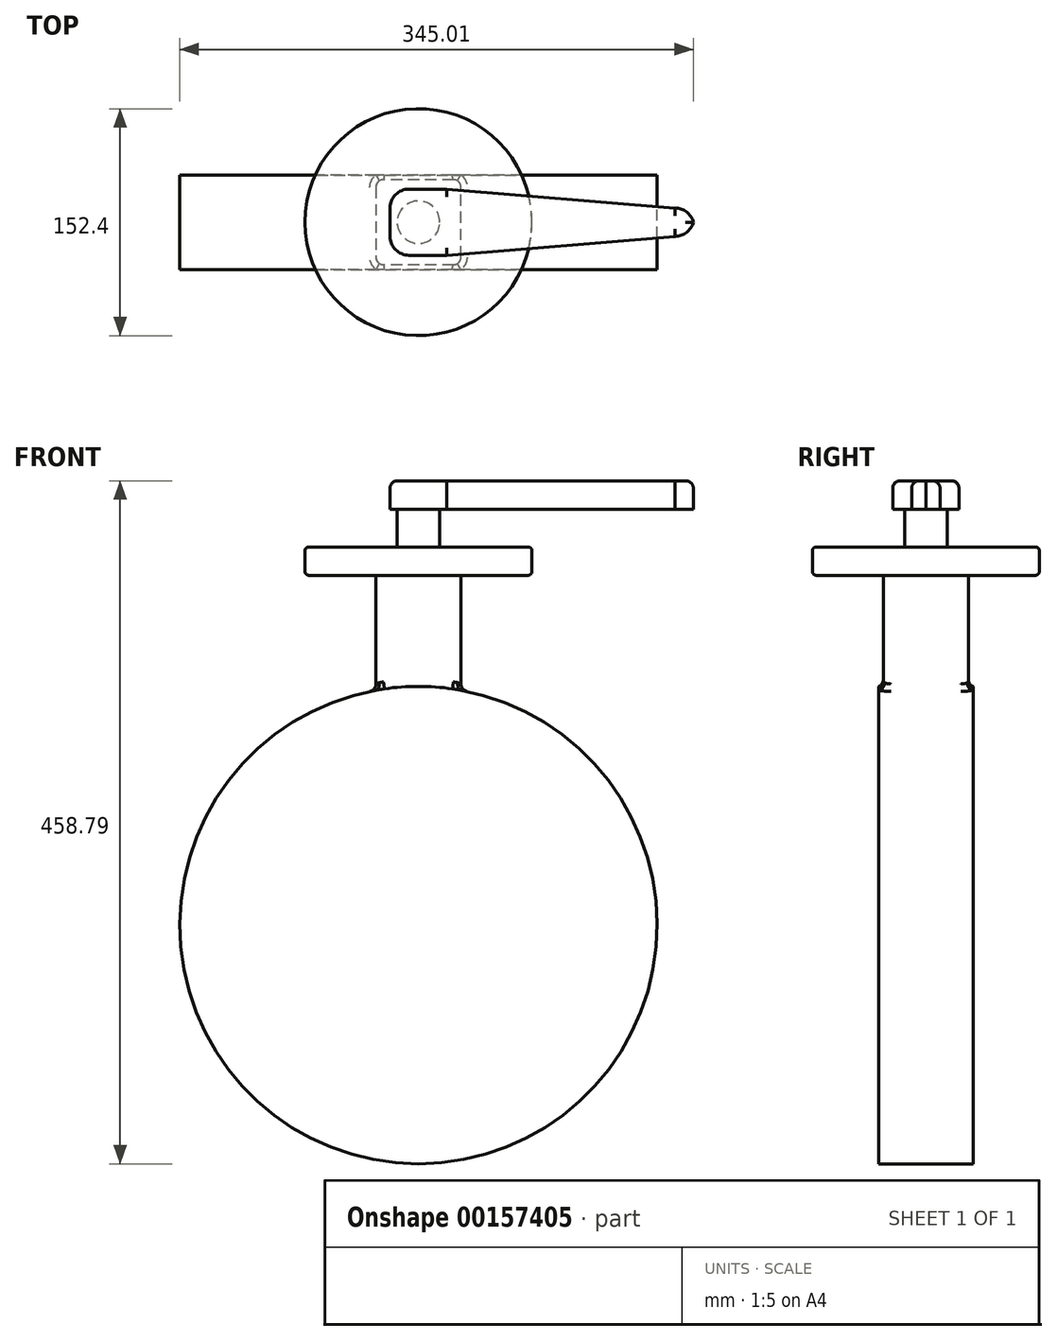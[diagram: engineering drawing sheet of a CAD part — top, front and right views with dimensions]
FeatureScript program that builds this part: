
annotation { "Feature Type Name" : "Feature", "Feature Type Description" : "" }
export const myFeature = defineFeature(function(context is Context, id is Id, definition is map)
    precondition{}
    {
        {
            var Q0;
            Q0=qCreatedBy(makeId("Front.planeOp"),FACE);
            var sketch = newSketch(context, id + "F0", { "sketchPlane" : qUnion([Q0])});
            skCircle(sketch, "E0", {"center": v(0, 0) * mm, "radius": 160.34 * mm});
            skSolve(sketch);
        }
        {
            var Q0;
            Q0 = qSketchRegion(id + "F0", true);
            extrude(context, id + "F1", {"entities" : qUnion([Q0]), "depth" : 63.5 * mm, "symmetric" : true});
        }
        {
            var Q0;
            Q0=qCreatedBy(makeId("Top.planeOp"),FACE);
            cPlane(context, id + "F2", {"entities" : qUnion([Q0]), "cplaneType" : CPlaneType.OFFSET, "offset" : 152.4 * mm, "width" : 152.4 * mm, "height" : 152.4 * mm});
        }
        {
            var Q0;
            Q0=qCreatedBy(id+"F2.planeOp",FACE);
            var sketch = newSketch(context, id + "F3", { "sketchPlane" : qUnion([Q0])});
            skLineSegment(sketch, "E1.bottom", {"start": v(28.58, 28.58) * mm, "end": v(-28.58, 28.58) * mm});
            skLineSegment(sketch, "E1.top", {"start": v(28.57, -28.58) * mm, "end": v(-28.58, -28.58) * mm});
            skLineSegment(sketch, "E1.left", {"start": v(28.58, 28.58) * mm, "end": v(28.57, -28.58) * mm});
            skLineSegment(sketch, "E1.right", {"start": v(-28.58, 28.58) * mm, "end": v(-28.58, -28.58) * mm});
            skPoint(sketch, "E1.middle", {"position": v(0, 0) * mm});
            skSolve(sketch);
        }
        {
            var Q0;
            Q0 = qSketchRegion(id + "F3", true);
            extrude(context, id + "F4", {"entities" : qUnion([Q0]), "operationType" : NewBodyOperationType.ADD, "depth" : 101.6 * mm});
        }
        {
            var Q0;
            Q0=makeQuery(id+"F4.opExtrude","CAP_FACE",FACE,{"disambiguationData":[OSD([sQuery(id+"F3.wireOp",EDGE,"E1.bottom"),sQuery(id+"F3.wireOp",EDGE,"E1.top"),sQuery(id+"F3.wireOp",EDGE,"E1.left"),sQuery(id+"F3.wireOp",EDGE,"E1.right")])],"isStart":false});
            var sketch = newSketch(context, id + "F5", { "sketchPlane" : qUnion([Q0])});
            skCircle(sketch, "E2", {"center": v(0, 0) * mm, "radius": 76.2 * mm});
            skSolve(sketch);
        }
        {
            var Q0;
            Q0 = qSketchRegion(id + "F5", true);
            extrude(context, id + "F6", {"entities" : qUnion([Q0]), "operationType" : NewBodyOperationType.ADD, "oppositeDirection" : true, "depth" : 19.05 * mm});
        }
        {
            var Q0;
            Q0=makeQuery(id+"F6.boolean.opBoolean","MERGE",FACE,{"derivedFrom":[makeQuery(id+"F4.opExtrude","CAP_FACE",FACE,{"disambiguationData":[OSD([sQuery(id+"F3.wireOp",EDGE,"E1.bottom"),sQuery(id+"F3.wireOp",EDGE,"E1.top"),sQuery(id+"F3.wireOp",EDGE,"E1.left"),sQuery(id+"F3.wireOp",EDGE,"E1.right")])],"isStart":false}),makeQuery(id+"F6.opExtrude","CAP_FACE",FACE,{"disambiguationData":[OSD([sQuery(id+"F5.wireOp",EDGE,"E2")])],"isStart":true})]});
            var sketch = newSketch(context, id + "F7", { "sketchPlane" : qUnion([Q0])});
            skCircle(sketch, "E3", {"center": v(0, 0) * mm, "radius": 14.29 * mm});
            skSolve(sketch);
        }
        {
            var Q0;
            Q0 = qSketchRegion(id + "F7", true);
            extrude(context, id + "F8", {"entities" : qUnion([Q0]), "operationType" : NewBodyOperationType.ADD, "depth" : 25.4 * mm});
        }
        {
            var Q0;
            Q0=makeQuery(id+"F8.opExtrude","CAP_FACE",FACE,{"disambiguationData":[OSD([sQuery(id+"F7.wireOp",EDGE,"E3")])],"isStart":false});
            var sketch = newSketch(context, id + "F9", { "sketchPlane" : qUnion([Q0])});
            skLineSegment(sketch, "E4.bottom", {"start": v(19.05, 22.22) * mm, "end": v(-19.05, 22.23) * mm});
            skLineSegment(sketch, "E4.top", {"start": v(19.05, -22.23) * mm, "end": v(-19.05, -22.22) * mm});
            skLineSegment(sketch, "E4.right", {"start": v(-19.05, 22.23) * mm, "end": v(-19.05, -22.22) * mm});
            skPoint(sketch, "E4.middle", {"position": v(0, 0) * mm});
            skLineSegment(sketch, "E5.bottom", {"start": v(172.38, 9.53) * mm, "end": v(185.08, 9.53) * mm});
            skLineSegment(sketch, "E5.top", {"start": v(172.38, -9.52) * mm, "end": v(185.08, -9.52) * mm});
            skLineSegment(sketch, "E5.right", {"start": v(185.08, 9.53) * mm, "end": v(185.08, -9.52) * mm});
            skPoint(sketch, "E5.middle", {"position": v(178.73, 0) * mm});
            skLineSegment(sketch, "E6", {"start": v(19.05, 22.22) * mm, "end": v(172.38, 9.53) * mm});
            skLineSegment(sketch, "E7", {"start": v(19.05, -22.23) * mm, "end": v(172.38, -9.52) * mm});
            skSolve(sketch);
        }
        {
            var Q0;
            Q0 = qSketchRegion(id + "F9", true);
            extrude(context, id + "F10", {"entities" : qUnion([Q0]), "operationType" : NewBodyOperationType.ADD, "depth" : 19.05 * mm});
        }
        {
            var Q0;
            Q0=makeQuery(id+"F10.opExtrude","SWEPT_EDGE",EDGE,{"disambiguationData":[OSD([sQuery(id+"F9.wireOp",EDGE,"E4.top"),sQuery(id+"F9.wireOp",EDGE,"E4.right")])]});
            var Q1;
            Q1=makeQuery(id+"F10.opExtrude","SWEPT_EDGE",EDGE,{"disambiguationData":[OSD([sQuery(id+"F9.wireOp",EDGE,"E5.top"),sQuery(id+"F9.wireOp",EDGE,"E5.right")])]});
            var Q2;
            Q2=makeQuery(id+"F10.opExtrude","SWEPT_EDGE",EDGE,{"disambiguationData":[OSD([sQuery(id+"F9.wireOp",EDGE,"E5.bottom"),sQuery(id+"F9.wireOp",EDGE,"E5.right")])]});
            var Q3;
            Q3=makeQuery(id+"F10.opExtrude","SWEPT_EDGE",EDGE,{"disambiguationData":[OSD([sQuery(id+"F9.wireOp",EDGE,"E4.bottom"),sQuery(id+"F9.wireOp",EDGE,"E4.right")])]});
            fillet(context, id + "F11", {"entities" : qUnion([Q0, Q1, Q2, Q3]), "radius" : 12.7 * mm, "tangentPropagation" : true, "allowEdgeOverflow" : false});
        }
        {
            var Q0;
            Q0=makeQuery(id+"F10.opExtrude","CAP_EDGE",EDGE,{"disambiguationData":[OSD([sQuery(id+"F9.wireOp",EDGE,"E7")])],"isStart":false});
            var Q1;
            Q1=makeQuery(id+"F10.opExtrude","CAP_EDGE",EDGE,{"disambiguationData":[OSD([sQuery(id+"F9.wireOp",EDGE,"E6")])],"isStart":false});
            var Q2;
            {var subQ0=sQuery(id+"F9.wireOp",EDGE,"E5.right");var subQ1=sQuery(id+"F9.wireOp",EDGE,"E5.bottom");Q2=makeQuery(id+"F11.opFillet","BLEND_EDGE",EDGE,{"blendedFrom":[makeQuery(id+"F10.opExtrude","SWEPT_EDGE",EDGE,{"disambiguationData":[OSD([subQ1,subQ0])]}),makeQuery(id+"F10.opExtrude","CAP_FACE",FACE,{"disambiguationData":[OSD([sQuery(id+"F9.wireOp",EDGE,"E4.bottom"),sQuery(id+"F9.wireOp",EDGE,"E4.top"),sQuery(id+"F9.wireOp",EDGE,"E4.right"),subQ1,sQuery(id+"F9.wireOp",EDGE,"E5.top"),subQ0,sQuery(id+"F9.wireOp",EDGE,"E6"),sQuery(id+"F9.wireOp",EDGE,"E7")])],"isStart":false})],"blendedInto":[makeQuery(id+"F10.opExtrude","CAP_FACE",FACE,{"disambiguationData":[OSD([sQuery(id+"F9.wireOp",EDGE,"E4.bottom"),sQuery(id+"F9.wireOp",EDGE,"E4.top"),sQuery(id+"F9.wireOp",EDGE,"E4.right"),subQ1,sQuery(id+"F9.wireOp",EDGE,"E5.top"),subQ0,sQuery(id+"F9.wireOp",EDGE,"E6"),sQuery(id+"F9.wireOp",EDGE,"E7")])],"isStart":false})]});}
            var Q3;
            {var subQ0=sQuery(id+"F9.wireOp",EDGE,"E5.right");var subQ1=sQuery(id+"F9.wireOp",EDGE,"E5.top");Q3=makeQuery(id+"F11.opFillet","BLEND_EDGE",EDGE,{"blendedFrom":[makeQuery(id+"F10.opExtrude","SWEPT_EDGE",EDGE,{"disambiguationData":[OSD([subQ1,subQ0])]}),makeQuery(id+"F10.opExtrude","CAP_FACE",FACE,{"disambiguationData":[OSD([sQuery(id+"F9.wireOp",EDGE,"E4.bottom"),sQuery(id+"F9.wireOp",EDGE,"E4.top"),sQuery(id+"F9.wireOp",EDGE,"E4.right"),sQuery(id+"F9.wireOp",EDGE,"E5.bottom"),subQ1,subQ0,sQuery(id+"F9.wireOp",EDGE,"E6"),sQuery(id+"F9.wireOp",EDGE,"E7")])],"isStart":false})],"blendedInto":[makeQuery(id+"F10.opExtrude","CAP_FACE",FACE,{"disambiguationData":[OSD([sQuery(id+"F9.wireOp",EDGE,"E4.bottom"),sQuery(id+"F9.wireOp",EDGE,"E4.top"),sQuery(id+"F9.wireOp",EDGE,"E4.right"),sQuery(id+"F9.wireOp",EDGE,"E5.bottom"),subQ1,subQ0,sQuery(id+"F9.wireOp",EDGE,"E6"),sQuery(id+"F9.wireOp",EDGE,"E7")])],"isStart":false})]});}
            var Q4;
            {var subQ0=sQuery(id+"F9.wireOp",EDGE,"E4.right");var subQ1=sQuery(id+"F9.wireOp",EDGE,"E4.top");Q4=makeQuery(id+"F11.opFillet","BLEND_EDGE",EDGE,{"blendedFrom":[makeQuery(id+"F10.opExtrude","SWEPT_EDGE",EDGE,{"disambiguationData":[OSD([subQ1,subQ0])]}),makeQuery(id+"F10.opExtrude","CAP_FACE",FACE,{"disambiguationData":[OSD([sQuery(id+"F9.wireOp",EDGE,"E4.bottom"),subQ1,subQ0,sQuery(id+"F9.wireOp",EDGE,"E5.bottom"),sQuery(id+"F9.wireOp",EDGE,"E5.top"),sQuery(id+"F9.wireOp",EDGE,"E5.right"),sQuery(id+"F9.wireOp",EDGE,"E6"),sQuery(id+"F9.wireOp",EDGE,"E7")])],"isStart":false})],"blendedInto":[makeQuery(id+"F10.opExtrude","CAP_FACE",FACE,{"disambiguationData":[OSD([sQuery(id+"F9.wireOp",EDGE,"E4.bottom"),subQ1,subQ0,sQuery(id+"F9.wireOp",EDGE,"E5.bottom"),sQuery(id+"F9.wireOp",EDGE,"E5.top"),sQuery(id+"F9.wireOp",EDGE,"E5.right"),sQuery(id+"F9.wireOp",EDGE,"E6"),sQuery(id+"F9.wireOp",EDGE,"E7")])],"isStart":false})]});}
            fillet(context, id + "F12", {"entities" : qUnion([Q0, Q1, Q2, Q3, Q4]), "radius" : 5.08 * mm, "tangentPropagation" : true, "allowEdgeOverflow" : false});
        }
        {
            var Q0;
            Q0=makeQuery(id+"F6.opExtrude","CAP_EDGE",EDGE,{"disambiguationData":[OSD([sQuery(id+"F5.wireOp",EDGE,"E2")])],"isStart":true});
            var Q1;
            Q1=makeQuery(id+"F6.opExtrude","CAP_EDGE",EDGE,{"disambiguationData":[OSD([sQuery(id+"F5.wireOp",EDGE,"E2")])],"isStart":false});
            fillet(context, id + "F13", {"entities" : qUnion([Q0, Q1]), "radius" : 2.54 * mm, "tangentPropagation" : true, "allowEdgeOverflow" : false});
        }
        {
            var Q0;
            Q0=makeQuery(id+"F4.opExtrude","SWEPT_EDGE",EDGE,{"disambiguationData":[OSD([sQuery(id+"F3.wireOp",EDGE,"E1.top"),sQuery(id+"F3.wireOp",EDGE,"E1.right")])]});
            var Q1;
            Q1=makeQuery(id+"F4.opExtrude","SWEPT_EDGE",EDGE,{"disambiguationData":[OSD([sQuery(id+"F3.wireOp",EDGE,"E1.bottom"),sQuery(id+"F3.wireOp",EDGE,"E1.right")])]});
            var Q2;
            Q2=makeQuery(id+"F4.opExtrude","SWEPT_EDGE",EDGE,{"disambiguationData":[OSD([sQuery(id+"F3.wireOp",EDGE,"E1.top"),sQuery(id+"F3.wireOp",EDGE,"E1.left")])]});
            var Q3;
            Q3=makeQuery(id+"F4.opExtrude","SWEPT_EDGE",EDGE,{"disambiguationData":[OSD([sQuery(id+"F3.wireOp",EDGE,"E1.bottom"),sQuery(id+"F3.wireOp",EDGE,"E1.left")])]});
            fillet(context, id + "F14", {"entities" : qUnion([Q0, Q1, Q2, Q3]), "radius" : 5.08 * mm, "tangentPropagation" : true, "allowEdgeOverflow" : false});
        }
        {
            var Q0;
            Q0=makeQuery(id+"F4.boolean.opBoolean","INTERSECT",EDGE,{"derivedFrom":[makeQuery(id+"F1.opExtrude","SWEPT_FACE",FACE,{"disambiguationData":[OSD([sQuery(id+"F0.wireOp",EDGE,"E0")])]}),makeQuery(id+"F4.opExtrude","SWEPT_FACE",FACE,{"disambiguationData":[OSD([sQuery(id+"F3.wireOp",EDGE,"E1.right")])]})]});
            fillet(context, id + "F15", {"entities" : qUnion([Q0]), "radius" : 5.08 * mm, "tangentPropagation" : true, "allowEdgeOverflow" : false});
        }
    });
